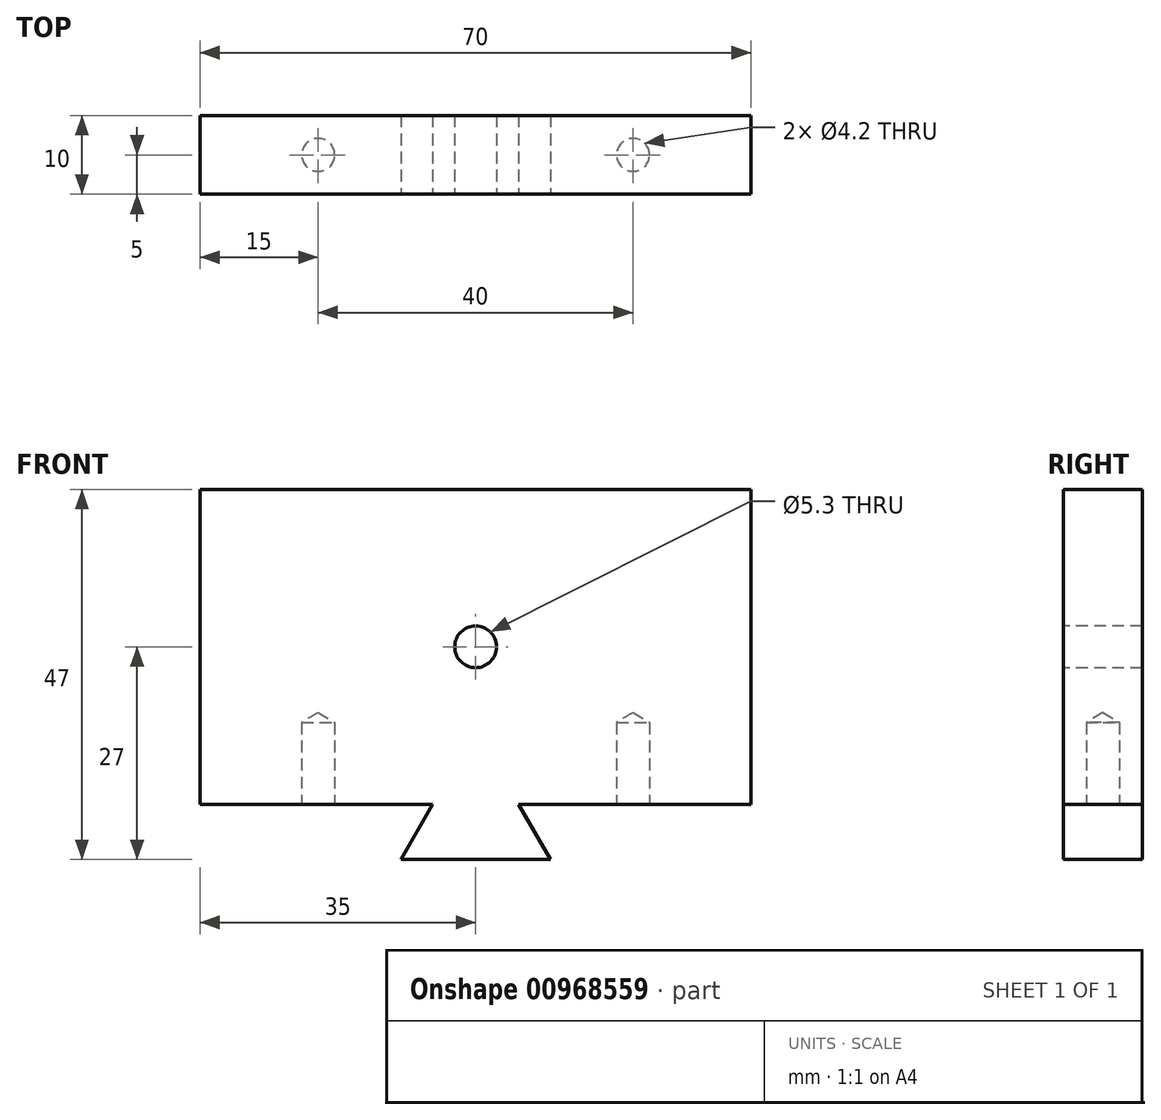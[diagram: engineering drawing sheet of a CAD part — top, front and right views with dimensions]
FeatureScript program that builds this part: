
annotation { "Feature Type Name" : "Feature", "Feature Type Description" : "" }
export const myFeature = defineFeature(function(context is Context, id is Id, definition is map)
    precondition{}
    {
        {
            var Q0;
            Q0=qCreatedBy(makeId("Front.planeOp"),FACE);
            var sketch = newSketch(context, id + "F0", { "sketchPlane" : qUnion([Q0])});
            skLineSegment(sketch, "E0", {"start": v(35, 0) * mm, "end": v(35, 20) * mm});
            skLineSegment(sketch, "E1.bottom", {"start": v(35, 20) * mm, "end": v(-35, 20) * mm});
            skLineSegment(sketch, "E1.top", {"start": v(35, -20) * mm, "end": v(5.46, -20) * mm});
            skLineSegment(sketch, "E1.left", {"start": v(35, 20) * mm, "end": v(35, -20) * mm});
            skLineSegment(sketch, "E1.right", {"start": v(-35, 20) * mm, "end": v(-35, -20) * mm});
            skLineSegment(sketch, "E2", {"start": v(0, -27) * mm, "end": v(9.5, -27) * mm});
            skLineSegment(sketch, "E3", {"start": v(0, -27) * mm, "end": v(-9.5, -27) * mm});
            skLineSegment(sketch, "E4", {"start": v(-9.5, -27) * mm, "end": v(-5.46, -20) * mm});
            skLineSegment(sketch, "E5", {"start": v(9.5, -27) * mm, "end": v(5.46, -20) * mm});
            skLineSegment(sketch, "E6.trimOffspring", {"start": v(-5.46, -20) * mm, "end": v(-35, -20) * mm});
            skPoint(sketch, "E7.orphan", {"position": v(0, -20) * mm});
            skPoint(sketch, "E8", {"position": v(0, 0) * mm});
            skSolve(sketch);
        }
        {
            var Q0;
            {var subQ1=sQuery(id+"F0.wireOp",EDGE,"E1.bottom");Q0=makeQuery(id+"F0.imprint","IMPRINT",FACE,{"disambiguationData":[TD([[makeQuery(id+"F0.imprint","IMPRINT",EDGE,{"derivedFrom":subQ1}),1.0]])]});}
            extrude(context, id + "F1", {"entities" : qUnion([Q0]), "oppositeDirection" : true, "depth" : 10 * mm, "offsetDistance" : 25 * mm});
        }
        {
            var Q0;
            Q0=sQuery(id+"F0.wireOp",VERTEX,"E8");
            var Q1;
            Q1=makeQuery(id+"F1.opExtrude","SWEPT_BODY",BODY,{"disambiguationData":[OSD([sQuery(id+"F0.wireOp",EDGE,"E1.bottom"),sQuery(id+"F0.wireOp",EDGE,"E1.top"),sQuery(id+"F0.wireOp",EDGE,"E1.left"),sQuery(id+"F0.wireOp",EDGE,"E1.right"),sQuery(id+"F0.wireOp",EDGE,"E2"),sQuery(id+"F0.wireOp",EDGE,"E3"),sQuery(id+"F0.wireOp",EDGE,"E4"),sQuery(id+"F0.wireOp",EDGE,"E5"),sQuery(id+"F0.wireOp",EDGE,"E6.trimOffspring")])]});
            hole(context, id + "F2", {"style" : HoleStyle.SIMPLE, "endStyle" : HoleEndStyle.THROUGH, "standardTappedOrClearance" : lookupTablePath({ "fit" : "Close", "standard" : "ISO", "size" : "M5", "type" : "Clearance" }), "standardBlindInLast" : lookupTablePath({ "fit" : "Close", "standard" : "ISO", "engagement" : "75%", "pitch" : "0.8 mm", "size" : "M5", "type" : "Clearance & tapped" }), "holeDiameter" : 5.3 * mm, "majorDiameter" : 5 * mm, "tappedDepth" : 5 * mm, "tapClearance" : 3, "startFromSketch" : true, "locations" : qUnion([Q0]), "scope" : qUnion([Q1])});
        }
        {
            var Q0;
            Q0=makeQuery(id+"F1.opExtrude","SWEPT_FACE",FACE,{"disambiguationData":[OSD([sQuery(id+"F0.wireOp",EDGE,"E6.trimOffspring")])]});
            var sketch = newSketch(context, id + "F3", { "sketchPlane" : qUnion([Q0])});
            skCircle(sketch, "E9", {"center": v(-20, -5) * mm, "radius": 2.5 * mm});
            skCircle(sketch, "E10.MirrorC", {"center": v(20, -5) * mm, "radius": 2.5 * mm});
            skSolve(sketch);
        }
        {
            var Q0;
            Q0=sQuery(id+"F3.wireOp",VERTEX,"E9.center");
            var Q1;
            Q1=sQuery(id+"F3.wireOp",VERTEX,"E10.MirrorC.center");
            var Q2;
            Q2=makeQuery(id+"F1.opExtrude","SWEPT_BODY",BODY,{"disambiguationData":[OSD([sQuery(id+"F0.wireOp",EDGE,"E1.bottom"),sQuery(id+"F0.wireOp",EDGE,"E1.top"),sQuery(id+"F0.wireOp",EDGE,"E1.left"),sQuery(id+"F0.wireOp",EDGE,"E1.right"),sQuery(id+"F0.wireOp",EDGE,"E2"),sQuery(id+"F0.wireOp",EDGE,"E3"),sQuery(id+"F0.wireOp",EDGE,"E4"),sQuery(id+"F0.wireOp",EDGE,"E5"),sQuery(id+"F0.wireOp",EDGE,"E6.trimOffspring")])]});
            hole(context, id + "F4", {"style" : HoleStyle.SIMPLE, "endStyle" : HoleEndStyle.BLIND, "standardTappedOrClearance" : lookupTablePath({ "standard" : "ISO", "engagement" : "75%", "pitch" : "0.8 mm", "size" : "M5", "type" : "Tapped" }), "standardBlindInLast" : lookupTablePath({ "standard" : "ISO", "fit" : "Normal", "engagement" : "75%", "pitch" : "0.8 mm", "size" : "M5", "type" : "Clearance & tapped" }), "holeDiameter" : 4.2 * mm, "majorDiameter" : 5 * mm, "showTappedDepth" : true, "holeDepth" : 10.4 * mm, "isTappedThrough" : true, "tappedDepth" : 8 * mm, "tapClearance" : 3, "locations" : qUnion([Q0, Q1]), "scope" : qUnion([Q2])});
        }
    });
